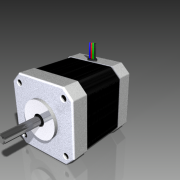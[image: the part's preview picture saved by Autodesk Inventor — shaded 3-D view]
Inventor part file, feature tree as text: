
AUTODESK INVENTOR PART (.ipt)
format: ipt  version: 2013 (Build 170138000, 138)  size: 1,076,224 bytes
history: native  units: mm
features: extrude x12, sketch x4, hole x4, fillet x4, chamfer x2, plane x1, pattern_linear x1, projected_geometry x1
ambient origin geometry x8: Origin, YZ Plane, XZ Plane, XY Plane, X Axis, Y Axis, Z Axis, Center Point
bodies: Solid1 (feature_tree)
feature tree (29):
  sketch  "Sketch1"  dims[d0=7.0mm d1=22.0mm]
  extrude  "Extrusion1"  Depth=22.0mm
  extrude  "Extrusion2"  Depth=31.0mm
  extrude  "Extrusion3"  Depth=3.0mm
  plane  "Work Plane2"
  extrude  "Extrusion7"  Depth=3.0mm
  extrude  "Extrusion8"  Depth=3.0mm
  chamfer  "Chamfer1"  Distance=42.0mm
  pattern_linear  "Rectangular Pattern2"  Spacing1=42.0mm  [1 undecoded]
  hole  "Hole1"  [1 undecoded]
  hole  "Hole2"  [1 undecoded]
  hole  "Hole3"  [1 undecoded]
  hole  "Hole4"  [1 undecoded]
  extrude  "Extrusion9"  Depth=25.809398mm
  fillet  "Fillet1"  Radius=24.0mm
  fillet  "Fillet2"  Radius=2.0mm
  chamfer  "Chamfer2"  Distance=48.0mm
  fillet  "Fillet3"  [1 undecoded]
  sketch  "Sketch6"  dims[d10=3.0mm d11=3.0mm d12=3.0mm d39=42.0mm d40=42.0mm d41=135.0deg d42=51.618795mm d43=51.618795mm d44=25.809398mm d45=25.809398mm d46=24.0mm d47=0.0mm d48=2.0mm d49=0.0mm d50=48.0mm d51=0.0mm d60=-10.0mm d126=28.0mm d127=0.0mm d128=1.0mm d129=1.0mm d130=1.0mm d131=1.0mm d132=0.5mm d134=0.5mm d135=0.5mm d136=0.5mm d137=0.5mm d138=1.0mm d139=1.0mm d140=0.5mm d141=0.0mm d145=0.125mm d146=2.0mm d147=45.0deg d148=560.0mm d150=0.5mm d151=10.0mm d152=10.0mm d153=6.0mm d154=6.0mm d155=4.0mm d156=2.0mm d157=90.0deg d158=3.0mm d159=0.0mm d160=10.0mm d161=10.0mm d162=6.0mm d163=6.0mm d164=4.0mm d165=2.0mm d166=90.0deg d167=3.0mm d168=0.0mm d169=10.0mm d170=10.0mm d171=6.0mm d172=6.0mm d173=4.0mm d174=2.0mm d175=90.0deg d176=3.0mm d177=0.0mm d178=10.0mm d179=10.0mm d180=6.0mm d181=6.0mm d182=4.0mm d183=2.0mm d184=90.0deg d185=3.0mm d186=0.0mm d187=48.0mm d188=0.0mm d189=47.0mm d190=0.0mm d191=1.0mm d192=1.0mm d193=0.5mm d194=2.0mm d195=45.0deg d196=0.5mm d197=1.2mm d198=40.0mm d200=1.2mm d201=10.0mm d203=10.0mm d205=2.5mm d206=2.5mm d207=1.0mm d208=0.0mm d209=0.3mm d210=10.0mm d211=0.0mm d212=10.0mm d213=0.0mm d214=10.0mm d215=0.0mm d216=10.0mm d217=0.0mm d218=0.2mm d219=5.0mm d220=0.0mm d221=0.0mm]
  extrude  "Extrusion10"  Depth=28.0mm TaperAngle=0.0deg
  fillet  "Fillet4"  Radius=1.0mm
  extrude  "Extrusion11"  Depth=1.0mm
  extrude  "Extrusion12"  Depth=0.5mm
  extrude  "Extrusion13"  Depth=0.5mm
  extrude  "Extrusion14"  Depth=0.5mm
  extrude  "Extrusion15"  Depth=0.5mm
  sketch  "Sketch4"  dims[d4=5.0mm d5=31.0mm]
  projected_geometry  "Projected Loop2"
  sketch  "Sketch5"  dims[d6=31.0mm d9=3.0mm]
note: 6 required parameter values undecoded (feature->parameter linkage not recoverable at this tier; creation-order binding heuristic only, values carry confidence <= 0.55)
